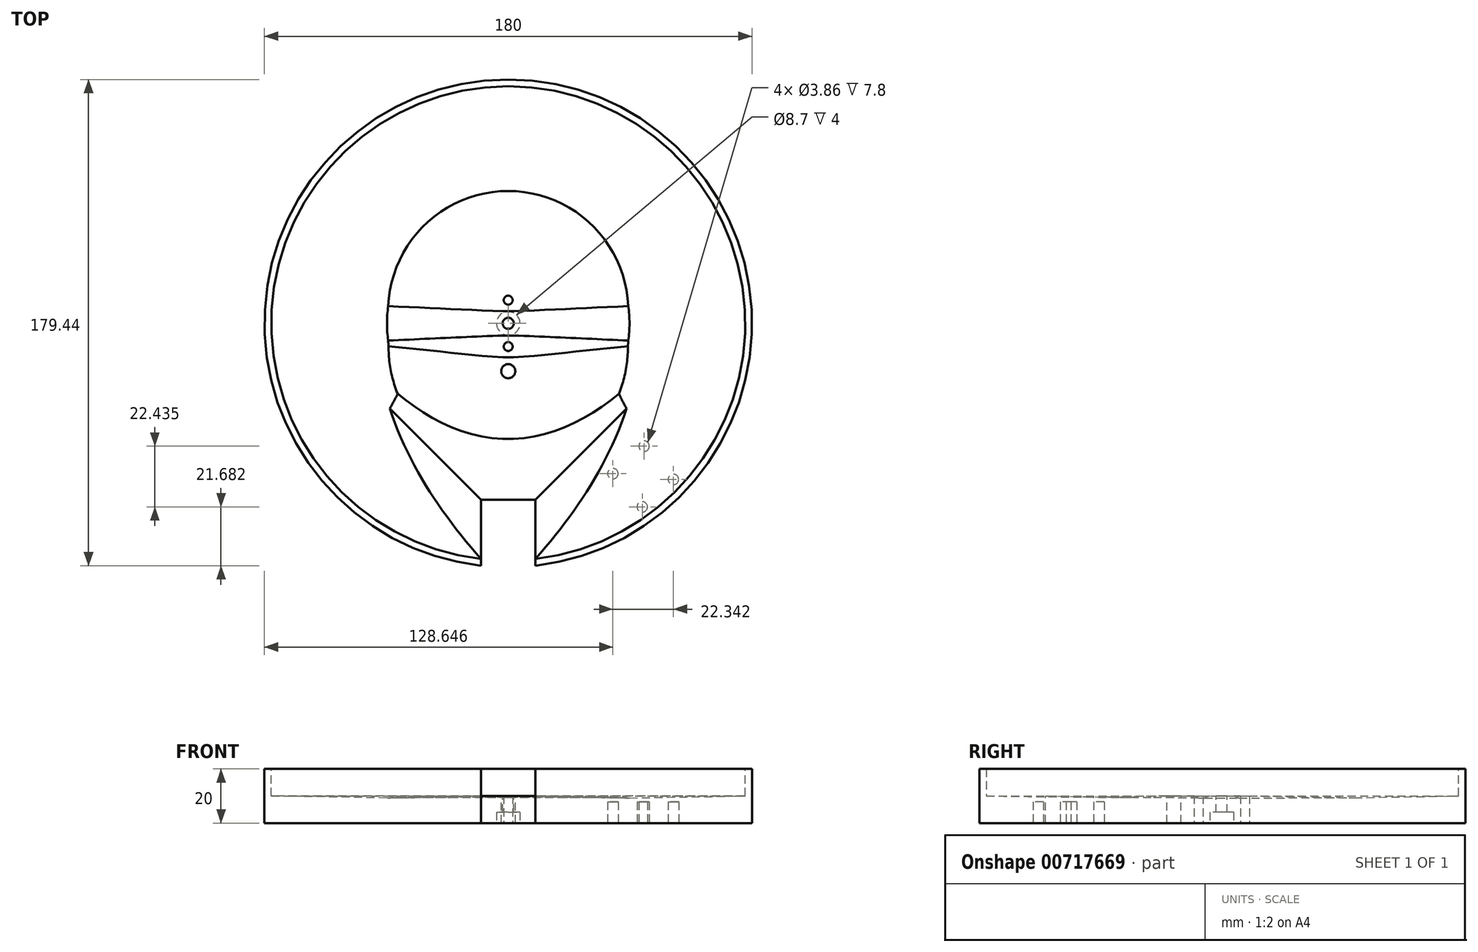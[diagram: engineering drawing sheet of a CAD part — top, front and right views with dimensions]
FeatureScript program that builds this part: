
annotation { "Feature Type Name" : "Feature", "Feature Type Description" : "" }
export const myFeature = defineFeature(function(context is Context, id is Id, definition is map)
    precondition{}
    {
        {
            var Q0;
            Q0=qCreatedBy(makeId("Front.planeOp"),FACE);
            var sketch = newSketch(context, id + "F0", { "sketchPlane" : qUnion([Q0])});
            skCircle(sketch, "E0", {"center": v(0, 0) * mm, "radius": 90 * mm});
            skSolve(sketch);
        }
        {
            var Q0;
            Q0=makeQuery(id+"F0.imprint","IMPRINT",FACE,{"disambiguationData":[TD([[makeQuery(id+"F0.imprint","IMPRINT",EDGE,{"derivedFrom":sQuery(id+"F0.wireOp",EDGE,"E0")}),1.0]])]});
            extrude(context, id + "F1", {"entities" : qUnion([Q0]), "depth" : 20 * mm, "offsetDistance" : 25 * mm});
        }
        {
            var Q0;
            Q0=makeQuery(id+"F1.opExtrude","CAP_FACE",FACE,{"disambiguationData":[OSD([sQuery(id+"F0.wireOp",EDGE,"E0")])],"isStart":false});
            var sketch = newSketch(context, id + "F2", { "sketchPlane" : qUnion([Q0])});
            skCircle(sketch, "E1", {"center": v(0, 0) * mm, "radius": 87.5 * mm});
            skSolve(sketch);
        }
        {
            var Q0;
            Q0 = qSketchRegion(id + "F2", true);
            extrude(context, id + "F3", {"entities" : qUnion([Q0]), "operationType" : NewBodyOperationType.REMOVE, "oppositeDirection" : true, "depth" : 10 * mm, "offsetDistance" : 25 * mm});
        }
        {
            var Q0;
            Q0=makeQuery(id+"F3.boolean.opBoolean","COPY",FACE,{"derivedFrom":makeQuery(id+"F3.opExtrude","CAP_FACE",FACE,{"disambiguationData":[OSD([sQuery(id+"F2.wireOp",EDGE,"E1")])],"isStart":false})});
            var sketch = newSketch(context, id + "F4", { "sketchPlane" : qUnion([Q0])});
            skCircle(sketch, "E2", {"center": v(0, 0) * mm, "radius": 2.05 * mm});
            skSolve(sketch);
        }
        {
            var Q0;
            Q0 = qSketchRegion(id + "F4", true);
            extrude(context, id + "F5", {"entities" : qUnion([Q0]), "operationType" : NewBodyOperationType.REMOVE, "oppositeDirection" : true, "depth" : 20 * mm, "offsetDistance" : 25 * mm});
        }
        {
            var Q0;
            Q0=makeQuery(id+"F3.boolean.opBoolean","COPY",FACE,{"derivedFrom":makeQuery(id+"F3.opExtrude","CAP_FACE",FACE,{"disambiguationData":[OSD([sQuery(id+"F2.wireOp",EDGE,"E1")])],"isStart":false})});
            var sketch = newSketch(context, id + "F6", { "sketchPlane" : qUnion([Q0])});
            skLineSegment(sketch, "E3.bottom", {"start": v(10, -90.13) * mm, "end": v(-10, -90.13) * mm});
            skLineSegment(sketch, "E3.top", {"start": v(10, -65.13) * mm, "end": v(-10, -65.13) * mm});
            skLineSegment(sketch, "E3.left", {"start": v(10, -90.13) * mm, "end": v(10, -65.13) * mm});
            skLineSegment(sketch, "E3.right", {"start": v(-10, -90.13) * mm, "end": v(-10, -65.13) * mm});
            skPoint(sketch, "E3.middle", {"position": v(0, -77.63) * mm});
            skSolve(sketch);
        }
        {
            var Q0;
            Q0 = qSketchRegion(id + "F6", true);
            extrude(context, id + "F7", {"entities" : qUnion([Q0]), "operationType" : NewBodyOperationType.REMOVE, "oppositeDirection" : true, "depth" : 25 * mm, "offsetDistance" : 25 * mm});
        }
        {
            var Q0;
            Q0=makeQuery(id+"F7.boolean.opBoolean","COPY",FACE,{"derivedFrom":makeQuery(id+"F7.opExtrude","CAP_FACE",FACE,{"disambiguationData":[OSD([sQuery(id+"F6.wireOp",EDGE,"E3.bottom"),sQuery(id+"F6.wireOp",EDGE,"E3.top"),sQuery(id+"F6.wireOp",EDGE,"E3.left"),sQuery(id+"F6.wireOp",EDGE,"E3.right")])],"isStart":true})});
            var sketch = newSketch(context, id + "F8", { "sketchPlane" : qUnion([Q0])});
            skLineSegment(sketch, "E4.bottom", {"start": v(-10, -86.93) * mm, "end": v(10, -86.93) * mm});
            skLineSegment(sketch, "E4.top", {"start": v(-10, -90.96) * mm, "end": v(10, -90.96) * mm});
            skLineSegment(sketch, "E4.left", {"start": v(-10, -86.93) * mm, "end": v(-10, -90.96) * mm});
            skLineSegment(sketch, "E4.right", {"start": v(10, -86.93) * mm, "end": v(10, -90.96) * mm});
            skSolve(sketch);
        }
        {
            var Q0;
            Q0 = qSketchRegion(id + "F8", true);
            extrude(context, id + "F9", {"entities" : qUnion([Q0]), "operationType" : NewBodyOperationType.REMOVE, "oppositeDirection" : true, "depth" : 25 * mm, "offsetDistance" : 25 * mm});
        }
        {
            var Q0;
            Q0=makeQuery(id+"F1.opExtrude","CAP_FACE",FACE,{"disambiguationData":[OSD([sQuery(id+"F0.wireOp",EDGE,"E0")])],"isStart":true});
            var sketch = newSketch(context, id + "F10", { "sketchPlane" : qUnion([Q0])});
            skLineSegment(sketch, "E5", {"start": v(-59.5, -67.53) * mm, "end": v(0, 0) * mm});
            skLineSegment(sketch, "E6", {"start": v(0, 0) * mm, "end": v(-59.5, -67.53) * mm, "construction": true});
            skLineSegment(sketch, "E7", {"start": v(-34.42, -69.85) * mm, "end": v(-67.76, -40.47) * mm, "construction": true});
            skCircle(sketch, "E8", {"center": v(-49.48, -67.76) * mm, "radius": 1.93 * mm});
            skPoint(sketch, "E8.first.point", {"position": v(-50.1, -69.59) * mm});
            skPoint(sketch, "E8.second.point", {"position": v(-48.16, -69.17) * mm});
            skPoint(sketch, "E8.third.point", {"position": v(-50.48, -66.1) * mm});
            skCircle(sketch, "E9", {"center": v(-50.16, -45.32) * mm, "radius": 1.93 * mm});
            skPoint(sketch, "E9.first.point", {"position": v(-51.6, -46.6) * mm});
            skPoint(sketch, "E9.second.point", {"position": v(-51.89, -44.47) * mm});
            skPoint(sketch, "E9.third.point", {"position": v(-48.33, -45.95) * mm});
            skCircle(sketch, "E10", {"center": v(-60.99, -57.62) * mm, "radius": 1.93 * mm});
            skPoint(sketch, "E10.first.point", {"position": v(-62.4, -58.93) * mm});
            skPoint(sketch, "E10.second.point", {"position": v(-62.34, -56.24) * mm});
            skPoint(sketch, "E10.third.point", {"position": v(-59.4, -56.53) * mm});
            skCircle(sketch, "E11", {"center": v(-38.65, -55.46) * mm, "radius": 1.93 * mm});
            skPoint(sketch, "E11.first.point", {"position": v(-39.9, -56.94) * mm});
            skPoint(sketch, "E11.second.point", {"position": v(-38.4, -57.38) * mm});
            skPoint(sketch, "E11.third.point", {"position": v(-38.56, -53.54) * mm});
            skSolve(sketch);
        }
        {
            var Q0;
            Q0 = qSketchRegion(id + "F10", true);
            extrude(context, id + "F11", {"entities" : qUnion([Q0]), "operationType" : NewBodyOperationType.REMOVE, "oppositeDirection" : true, "depth" : 7.8 * mm, "offsetDistance" : 25 * mm});
        }
        {
            var Q0;
            Q0=makeQuery(id+"F3.boolean.opBoolean","COPY",FACE,{"derivedFrom":makeQuery(id+"F3.opExtrude","CAP_FACE",FACE,{"disambiguationData":[OSD([sQuery(id+"F2.wireOp",EDGE,"E1")])],"isStart":false})});
            var sketch = newSketch(context, id + "F12", { "sketchPlane" : qUnion([Q0])});
            skArc(sketch, "E12.0", {"start": v(10, -89.44) * mm, "mid": v(0, 90) * mm, "end": v(-10, -89.44) * mm});
            skCircle(sketch, "E13", {"center": v(0, -17.66) * mm, "radius": 2.6 * mm});
            skSolve(sketch);
        }
        {
            var Q0;
            Q0 = qSketchRegion(id + "F12", true);
            extrude(context, id + "F13", {"entities" : qUnion([Q0]), "operationType" : NewBodyOperationType.REMOVE, "oppositeDirection" : true, "depth" : 25 * mm, "offsetDistance" : 25 * mm});
        }
        {
            var Q0;
            Q0=makeQuery(id+"F1.opExtrude","CAP_FACE",FACE,{"disambiguationData":[OSD([sQuery(id+"F0.wireOp",EDGE,"E0")])],"isStart":true});
            var sketch = newSketch(context, id + "F14", { "sketchPlane" : qUnion([Q0])});
            skCircle(sketch, "E14", {"center": v(0, 0) * mm, "radius": 4.35 * mm});
            skCircle(sketch, "E15", {"center": v(0, -8.56) * mm, "radius": 1.65 * mm});
            skCircle(sketch, "E16", {"center": v(0, 8.56) * mm, "radius": 1.65 * mm});
            skSolve(sketch);
        }
        {
            var Q0;
            Q0 = qSketchRegion(id + "F14", true);
            extrude(context, id + "F15", {"entities" : qUnion([Q0]), "operationType" : NewBodyOperationType.REMOVE, "oppositeDirection" : true, "depth" : 4 * mm, "offsetDistance" : 25 * mm});
        }
        {
            var Q0;
            Q0=qCreatedBy(makeId("Front.planeOp"),FACE);
            var sketch = newSketch(context, id + "F16", { "sketchPlane" : qUnion([Q0])});
            skLineSegment(sketch, "E17", {"start": v(0, 120.79) * mm, "end": v(0, -107.96) * mm, "construction": true});
            skLineSegment(sketch, "E18", {"start": v(-111.44, 0) * mm, "end": v(110.44, 0) * mm, "construction": true});
            skSolve(sketch);
        }
        {
            var Q0;
            Q0=makeQuery(id+"F15.boolean.opBoolean","COPY",FACE,{"derivedFrom":makeQuery(id+"F15.opExtrude","CAP_FACE",FACE,{"disambiguationData":[OSD([sQuery(id+"F14.wireOp",EDGE,"E16")])],"isStart":false})});
            var Q1;
            Q1=makeQuery(id+"F15.boolean.opBoolean","COPY",FACE,{"derivedFrom":makeQuery(id+"F15.opExtrude","CAP_FACE",FACE,{"disambiguationData":[OSD([sQuery(id+"F14.wireOp",EDGE,"E15")])],"isStart":false})});
            extrude(context, id + "F17", {"entities" : qUnion([Q0, Q1]), "operationType" : NewBodyOperationType.REMOVE, "oppositeDirection" : true, "depth" : 25 * mm, "offsetDistance" : 25 * mm});
        }
        {
            var Q0;
            Q0=makeQuery(id+"F1.opExtrude","SWEPT_BODY",BODY,{"disambiguationData":[OSD([sQuery(id+"F0.wireOp",EDGE,"E0")])]});
            var Q1;
            Q1=sQuery(id+"F16.wireOp",EDGE,"E18");
            transform(context, id + "F18", {"entities" : qUnion([Q0]), "transformType" : TransformType.ROTATION, "transformAxis" : qUnion([Q1]), "angle" : 90 * degree, "oppositeDirection" : true, "makeCopy" : false});
        }
        {
            var Q0;
            Q0=makeQuery(id+"F3.boolean.opBoolean","COPY",FACE,{"derivedFrom":makeQuery(id+"F3.opExtrude","CAP_FACE",FACE,{"disambiguationData":[OSD([sQuery(id+"F2.wireOp",EDGE,"E1")])],"isStart":false})});
            extrude(context, id + "F19", {"entities" : qUnion([Q0]), "operationType" : NewBodyOperationType.REMOVE, "oppositeDirection" : true, "depth" : 0.8 * mm, "offsetDistance" : 25 * mm, "hasDraft" : true, "draftAngle" : 89 * degree, "draftPullDirection" : true});
        }
    });
